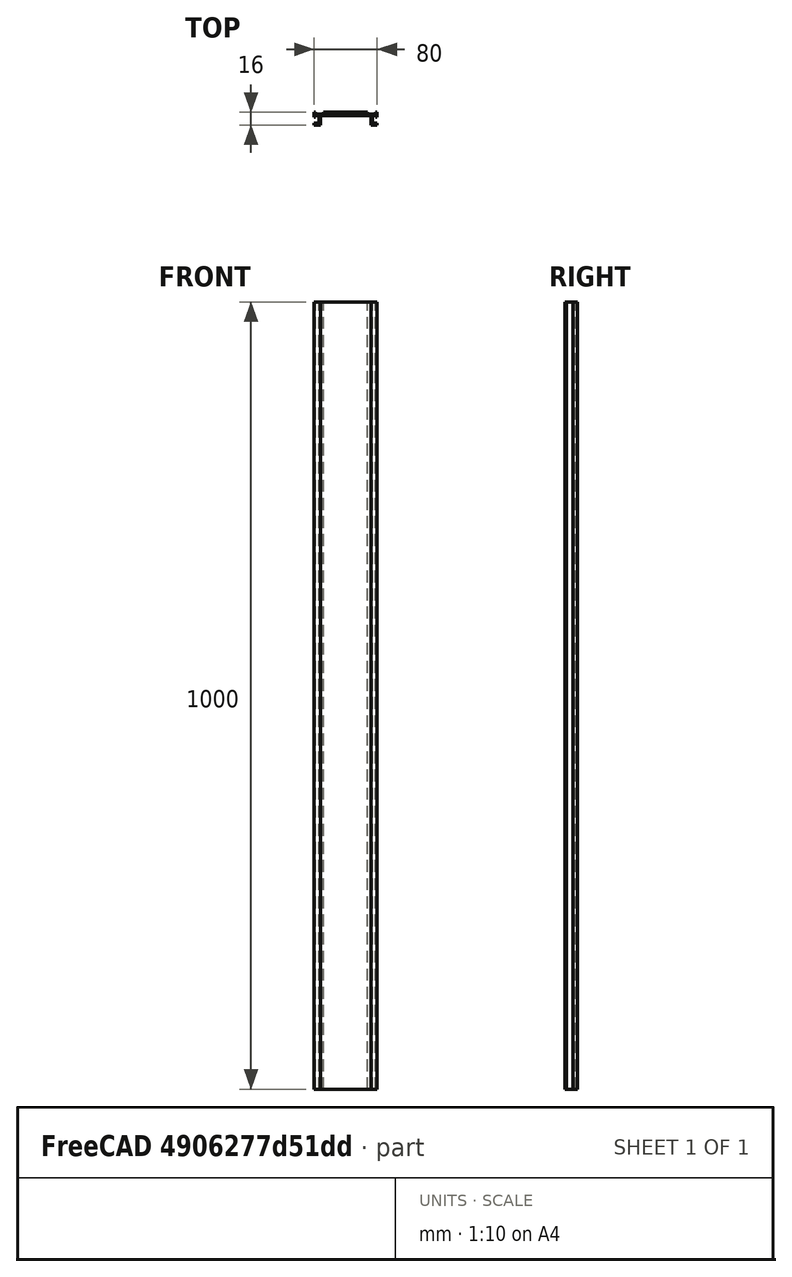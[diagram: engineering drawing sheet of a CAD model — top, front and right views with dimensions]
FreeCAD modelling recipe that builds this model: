
FCSTD DOCUMENT  (FreeCAD 0.18.4R)
Label: rails
License: All rights reserved
LicenseURL: http://en.wikipedia.org/wiki/All_rights_reserved
objects: Sketcher::SketchObject×1, PartDesign::Pad×1, PartDesign::Body×1
note: 4 computed .brp shape members not serialized (recipe doc carries the construction recipe); baked Part::Feature solids carry a one-line shape summary decoded from their .brp

FEATURE [Sketcher::SketchObject] Sketch
  MapMode = 5
  Support = -> [XY_Plane]
  sketch-geometry (30):
    g0: LineSegment StartX=0 StartY=2 StartZ=0 EndX=-28 EndY=2 EndZ=0
    g1: LineSegment StartX=-28 StartY=2 StartZ=0 EndX=-28 EndY=0 EndZ=0
    g2: LineSegment StartX=-28 StartY=0 StartZ=0 EndX=-38 EndY=0 EndZ=0
    g3: LineSegment StartX=-38 StartY=0 StartZ=0 EndX=-38 EndY=2 EndZ=0
    g4: LineSegment StartX=-38 StartY=2 StartZ=0 EndX=-40 EndY=2 EndZ=0
    g5: LineSegment StartX=-40 StartY=2 StartZ=0 EndX=-40 EndY=-4 EndZ=0
    g6: LineSegment StartX=-40 StartY=-4 StartZ=0 EndX=-38 EndY=-4 EndZ=0
    g7: LineSegment StartX=-38 StartY=-4 StartZ=0 EndX=-38 EndY=-2 EndZ=0
    g8: LineSegment StartX=-38 StartY=-2 StartZ=0 EndX=-34 EndY=-2 EndZ=0
    g9: LineSegment StartX=-34 StartY=-2 StartZ=0 EndX=-34 EndY=-12 EndZ=0
    g10: LineSegment StartX=-34 StartY=-12 StartZ=0 EndX=-40 EndY=-12 EndZ=0
    g11: LineSegment StartX=-40 StartY=-12 StartZ=0 EndX=-40 EndY=-14 EndZ=0
    g12: LineSegment StartX=-40 StartY=-14 StartZ=0 EndX=-32 EndY=-14 EndZ=0
    g13: LineSegment StartX=-32 StartY=-14 StartZ=0 EndX=-32 EndY=-2 EndZ=0
    g14: LineSegment StartX=-32 StartY=-2 StartZ=0 EndX=0 EndY=-2 EndZ=0
    g15: LineSegment StartX=0 StartY=2 StartZ=0 EndX=28 EndY=2 EndZ=0
    g16: LineSegment StartX=28 StartY=2 StartZ=0 EndX=28 EndY=0 EndZ=0
    g17: LineSegment StartX=28 StartY=0 StartZ=0 EndX=38 EndY=0 EndZ=0
    g18: LineSegment StartX=38 StartY=0 StartZ=0 EndX=38 EndY=2 EndZ=0
    g19: LineSegment StartX=38 StartY=2 StartZ=0 EndX=40 EndY=2 EndZ=0
    g20: LineSegment StartX=40 StartY=2 StartZ=0 EndX=40 EndY=-4 EndZ=0
    g21: LineSegment StartX=40 StartY=-4 StartZ=0 EndX=38 EndY=-4 EndZ=0
    g22: LineSegment StartX=38 StartY=-4 StartZ=0 EndX=38 EndY=-2 EndZ=0
    g23: LineSegment StartX=38 StartY=-2 StartZ=0 EndX=34 EndY=-2 EndZ=0
    g24: LineSegment StartX=34 StartY=-2 StartZ=0 EndX=34 EndY=-12 EndZ=0
    g25: LineSegment StartX=34 StartY=-12 StartZ=0 EndX=40 EndY=-12 EndZ=0
    g26: LineSegment StartX=40 StartY=-12 StartZ=0 EndX=40 EndY=-14 EndZ=0
    g27: LineSegment StartX=40 StartY=-14 StartZ=0 EndX=32 EndY=-14 EndZ=0
    g28: LineSegment StartX=32 StartY=-14 StartZ=0 EndX=32 EndY=-2 EndZ=0
    g29: LineSegment StartX=32 StartY=-2 StartZ=0 EndX=0 EndY=-2 EndZ=0
  constraints (24):
    c: Coincident(g0,g1)
    c: Coincident(g1,g2)
    c: Coincident(g2,g3)
    c: Coincident(g6,g7)
    c: Coincident(g7,g8)
    c: Coincident(g8,g9)
    c: Coincident(g9,g10)
    c: Coincident(g10,g11)
    c: Coincident(g11,g12)
    c: Coincident(g12,g13)
    c: Coincident(g13,g14)
    c: Coincident(g5,g6)
    c: Coincident(g15,g16)
    c: Coincident(g16,g17)
    c: Coincident(g17,g18)
    c: Coincident(g21,g22)
    c: Coincident(g22,g23)
    c: Coincident(g23,g24)
    c: Coincident(g24,g25)
    c: Coincident(g25,g26)
    c: Coincident(g26,g27)
    c: Coincident(g27,g28)
    c: Coincident(g28,g29)
    c: Coincident(g20,g21)
FEATURE [PartDesign::Pad] Pad
  Length = 1000
  Length2 = 100
  Profile = -> Sketch
  Type = 0
FEATURE [PartDesign::Body] Body
  Group = -> [Sketch,Pad]
  Origin = -> Origin
  Tip = -> Pad
